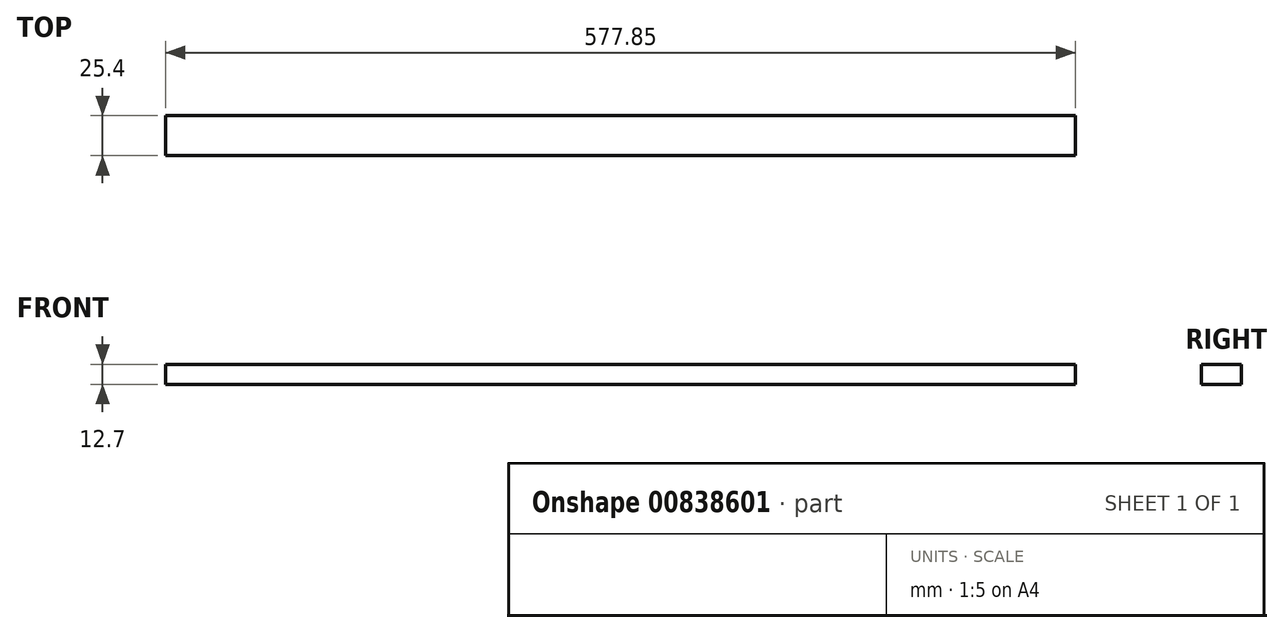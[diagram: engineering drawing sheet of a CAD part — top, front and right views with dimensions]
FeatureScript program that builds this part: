
annotation { "Feature Type Name" : "Feature", "Feature Type Description" : "" }
export const myFeature = defineFeature(function(context is Context, id is Id, definition is map)
    precondition{}
    {
        {
            var Q0;
            Q0=qCreatedBy(makeId("Front.planeOp"),FACE);
            var sketch = newSketch(context, id + "F0", { "sketchPlane" : qUnion([Q0])});
            skLineSegment(sketch, "E0.bottom", {"start": v(-289.84, 3.3) * mm, "end": v(288, 3.3) * mm});
            skLineSegment(sketch, "E0.top", {"start": v(-289.84, -9.4) * mm, "end": v(288, -9.4) * mm});
            skLineSegment(sketch, "E0.left", {"start": v(-289.84, 3.3) * mm, "end": v(-289.84, -9.4) * mm});
            skLineSegment(sketch, "E0.right", {"start": v(288, 3.3) * mm, "end": v(288, -9.4) * mm});
            skSolve(sketch);
        }
        {
            var Q0;
            Q0=makeQuery(id+"F0.imprint","IMPRINT",FACE,{"disambiguationData":[TD([[makeQuery(id+"F0.imprint","IMPRINT",EDGE,{"derivedFrom":sQuery(id+"F0.wireOp",EDGE,"E0.bottom")}),-1.0]])]});
            extrude(context, id + "F1", {"entities" : qUnion([Q0]), "depth" : 25.4 * mm, "offsetDistance" : 25.4 * mm});
        }
    });
